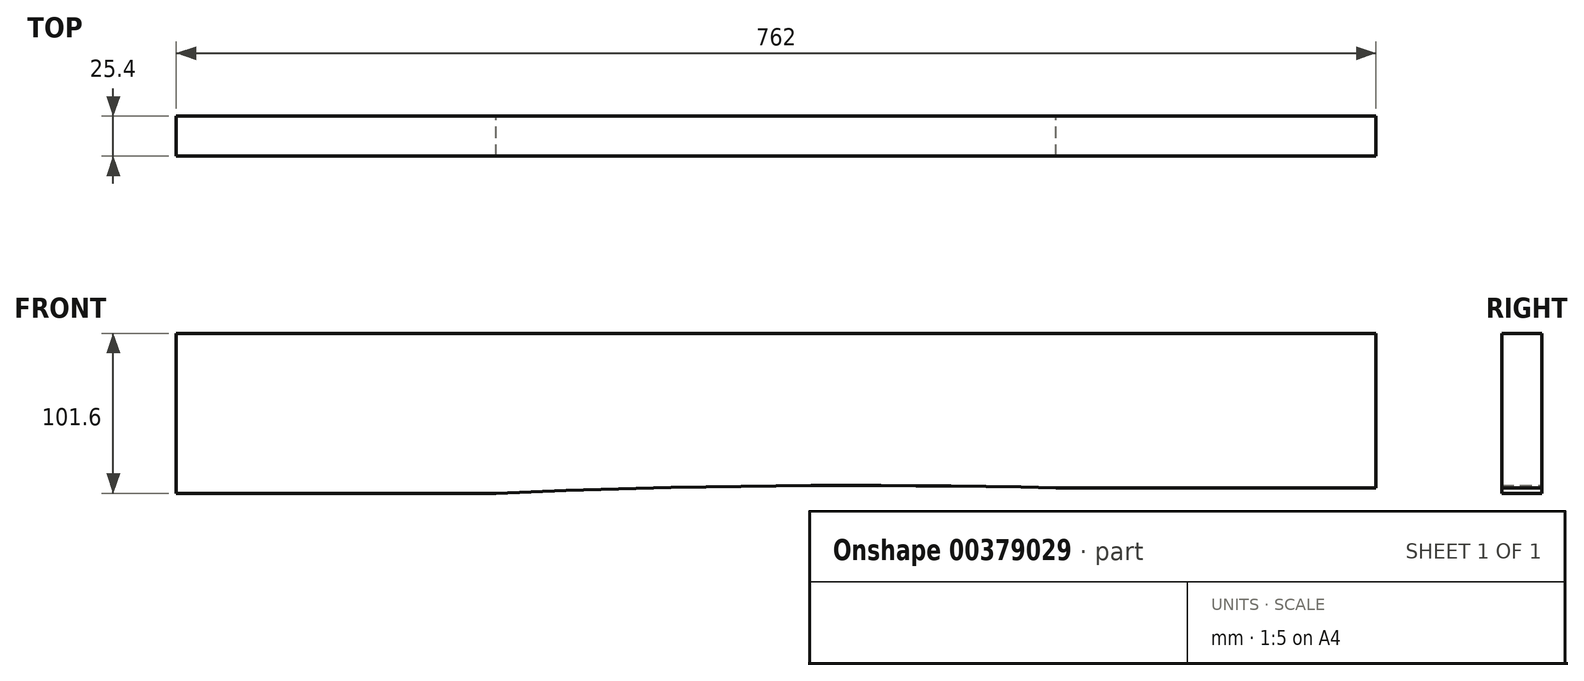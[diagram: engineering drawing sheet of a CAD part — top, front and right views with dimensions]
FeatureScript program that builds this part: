
annotation { "Feature Type Name" : "Feature", "Feature Type Description" : "" }
export const myFeature = defineFeature(function(context is Context, id is Id, definition is map)
    precondition{}
    {
        {
            var Q0;
            Q0=qCreatedBy(makeId("Front.planeOp"),FACE);
            var sketch = newSketch(context, id + "F0", { "sketchPlane" : qUnion([Q0])});
            skLineSegment(sketch, "E0", {"start": v(-813.58, 64.48) * mm, "end": v(-51.58, 64.48) * mm});
            skLineSegment(sketch, "E1", {"start": v(-813.58, 64.48) * mm, "end": v(-813.58, -37.12) * mm});
            skLineSegment(sketch, "E2", {"start": v(-51.58, 64.48) * mm, "end": v(-51.58, -33.69) * mm});
            skLineSegment(sketch, "E3", {"start": v(-610.38, -37.12) * mm, "end": v(-813.58, -37.12) * mm});
            skLineSegment(sketch, "E4", {"start": v(-51.58, -33.69) * mm, "end": v(-254.78, -33.69) * mm});
            skArc(sketch, "E5", {"start": v(-254.78, -33.69) * mm, "mid": v(-432.6, -32.45) * mm, "end": v(-610.38, -37.12) * mm});
            skSolve(sketch);
        }
        {
            var Q0;
            Q0=makeQuery(id+"F0.imprint","IMPRINT",FACE,{"disambiguationData":[TD([[makeQuery(id+"F0.imprint","IMPRINT",EDGE,{"derivedFrom":sQuery(id+"F0.wireOp",EDGE,"E0")}),-1.0]])]});
            extrude(context, id + "F1", {"entities" : qUnion([Q0]), "depth" : 25.4 * mm});
        }
    });
